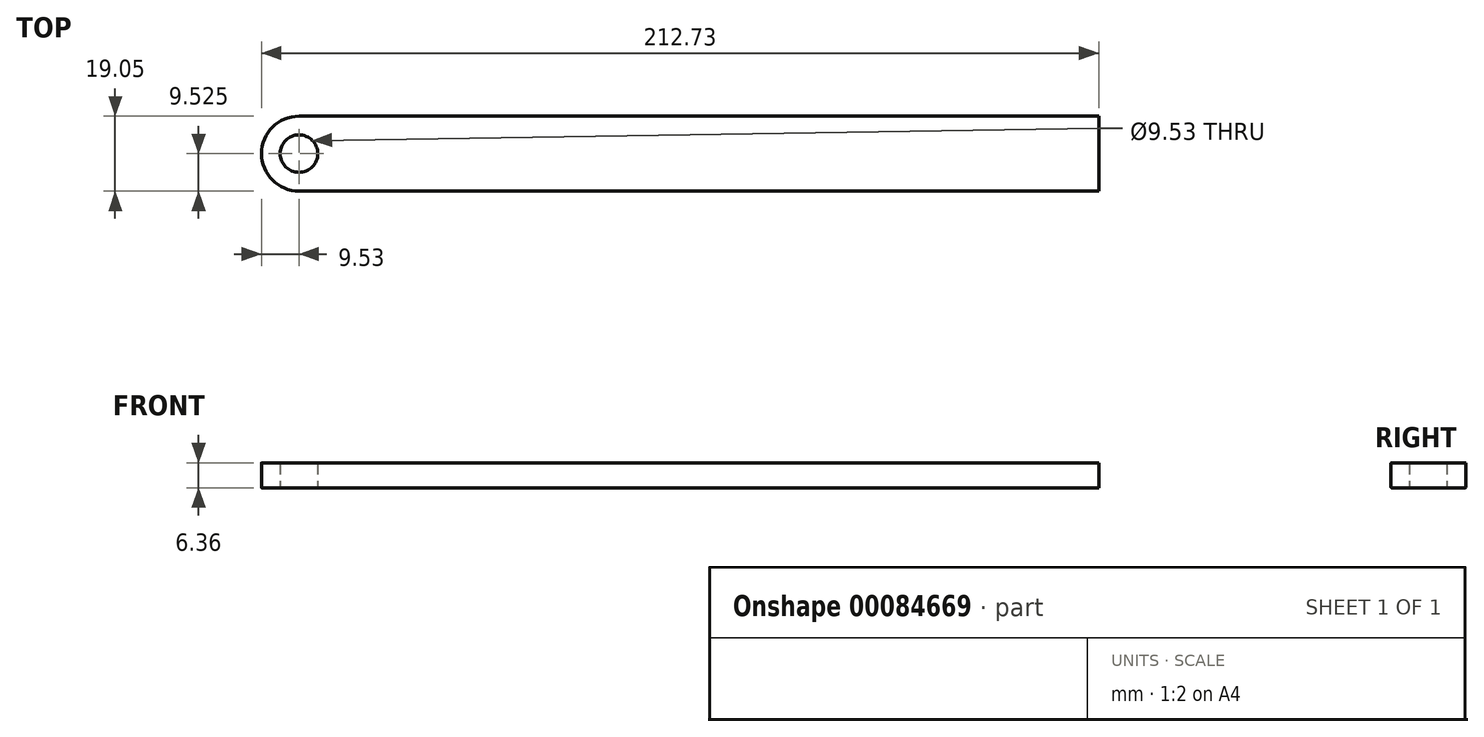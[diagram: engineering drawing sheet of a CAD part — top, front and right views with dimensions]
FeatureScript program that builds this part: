
annotation { "Feature Type Name" : "Feature", "Feature Type Description" : "" }
export const myFeature = defineFeature(function(context is Context, id is Id, definition is map)
    precondition{}
    {
        {
            var Q0;
            Q0=qCreatedBy(makeId("Top.planeOp"),FACE);
            var sketch = newSketch(context, id + "F0", { "sketchPlane" : qUnion([Q0])});
            skLineSegment(sketch, "E0", {"start": v(0, 0) * mm, "end": v(0, 19.05) * mm});
            skLineSegment(sketch, "E1", {"start": v(0, 19.05) * mm, "end": v(-203.2, 19.05) * mm});
            skLineSegment(sketch, "E2", {"start": v(0, 0) * mm, "end": v(-203.2, 0) * mm});
            skArc(sketch, "E3", {"start": v(-203.2, 19.05) * mm, "mid": v(-212.73, 9.52) * mm, "end": v(-203.2, 0) * mm});
            skCircle(sketch, "E4", {"center": v(-203.2, 9.52) * mm, "radius": 4.76 * mm});
            skSolve(sketch);
        }
        {
            assignVariable(context, id + "F1", {"name" : "FRadius", "anyValue" : .1});
        }
        {
            var Q0;
            Q0 = qSketchRegion(id + "F0", true);
            extrude(context, id + "F2", {"entities" : qUnion([Q0]), "endBound" : BoundingType.SYMMETRIC, "depth" : 6.35 * mm});
        }
        {
            var Q0;
            Q0=makeQuery(id+"F2.opExtrude","CAP_EDGE",EDGE,{"disambiguationData":[OSD([sQuery(id+"F0.wireOp",EDGE,"E2")])],"isStart":false});
            var Q1;
            Q1=makeQuery(id+"F2.opExtrude","CAP_EDGE",EDGE,{"disambiguationData":[OSD([sQuery(id+"F0.wireOp",EDGE,"E2")])],"isStart":true});
            fillet(context, id + "F3", {"entities" : qUnion([Q0, Q1]), "radius" : (getVariable(context, 'FRadius')) * mm, "tangentPropagation" : true, "allowEdgeOverflow" : false});
        }
    });
